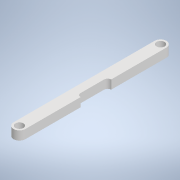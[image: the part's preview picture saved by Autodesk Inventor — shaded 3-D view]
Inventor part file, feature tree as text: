
AUTODESK INVENTOR PART (.ipt)
format: ipt  version: 2022.6 (Build 266554000, 554)  size: 121,856 bytes
history: native  units: mm
features: sketch x3, extrude x2, hole x1, projected_geometry x1
ambient origin geometry x8: Origin, YZ Plane, XZ Plane, XY Plane, X Axis, Y Axis, Z Axis, Center Point
bodies: Solid1 (feature_tree)
feature tree (7):
  extrude  "Extrusion1"  Depth=5.0mm
  hole  "Hole1"  [1 undecoded]
  extrude  "Extrusion2"  Depth=5.0mm
  sketch  "Sketch1"  dims[d0=60.0mm d1=5.0mm]
  sketch  "Sketch2"  dims[d2=3.75mm d3=0.0mm]
  projected_geometry  "Projected Loop1"
  sketch  "Sketch3"  dims[d4=3.4mm d5=6.0mm d6=6.0mm d7=2.0mm d8=90.0deg d9=8.0mm d10=20.594885mm d11=5.0mm d12=3.0mm d13=0.0mm d14=0.0mm]
note: 1 required parameter value undecoded (feature->parameter linkage not recoverable at this tier; creation-order binding heuristic only, values carry confidence <= 0.55)
